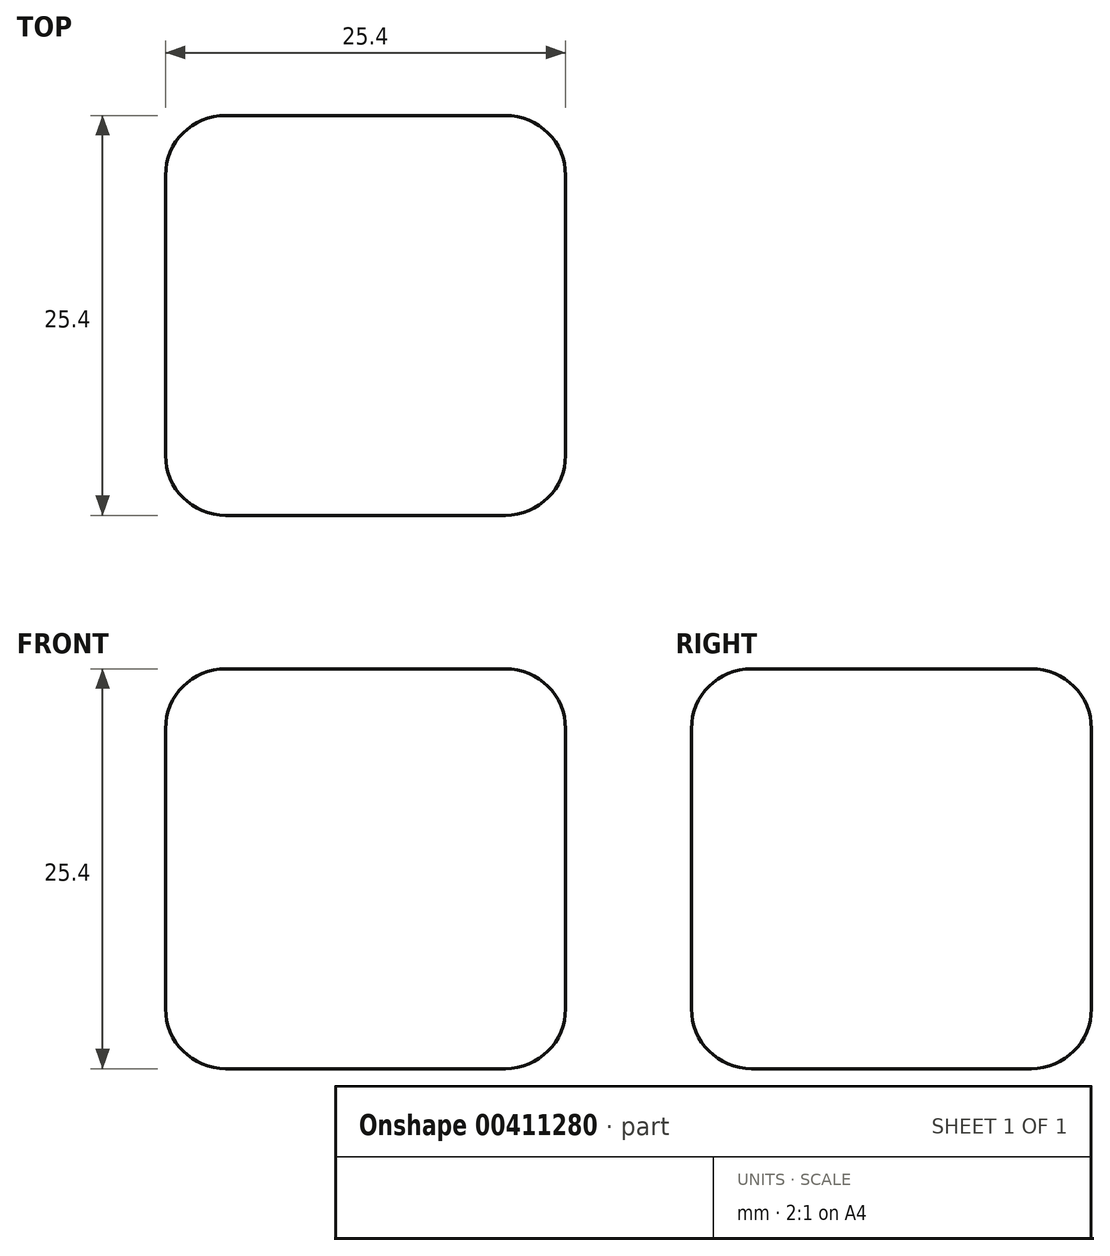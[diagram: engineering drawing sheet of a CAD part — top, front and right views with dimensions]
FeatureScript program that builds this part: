
annotation { "Feature Type Name" : "Feature", "Feature Type Description" : "" }
export const myFeature = defineFeature(function(context is Context, id is Id, definition is map)
    precondition{}
    {
        {
            var Q0;
            Q0=qCreatedBy(makeId("Top.planeOp"),FACE);
            var sketch = newSketch(context, id + "F0", { "sketchPlane" : qUnion([Q0])});
            skLineSegment(sketch, "E0.bottom", {"start": v(0, 0) * mm, "end": v(25.4, 0) * mm});
            skLineSegment(sketch, "E0.top", {"start": v(0, -25.4) * mm, "end": v(25.4, -25.4) * mm});
            skLineSegment(sketch, "E0.left", {"start": v(0, 0) * mm, "end": v(0, -25.4) * mm});
            skLineSegment(sketch, "E0.right", {"start": v(25.4, 0) * mm, "end": v(25.4, -25.4) * mm});
            skSolve(sketch);
        }
        {
            var Q0;
            Q0 = qSketchRegion(id + "F0", true);
            extrude(context, id + "F1", {"entities" : qUnion([Q0]), "depth" : 25.4 * mm});
        }
        {
            var Q0;
            Q0=makeQuery(id+"F1.opExtrude","SWEPT_EDGE",EDGE,{"disambiguationData":[OSD([sQuery(id+"F0.wireOp",EDGE,"E0.bottom"),sQuery(id+"F0.wireOp",EDGE,"E0.left")])]});
            var Q1;
            Q1=makeQuery(id+"F1.opExtrude","CAP_EDGE",EDGE,{"disambiguationData":[OSD([sQuery(id+"F0.wireOp",EDGE,"E0.bottom")])],"isStart":false});
            var Q2;
            Q2=makeQuery(id+"F1.opExtrude","CAP_EDGE",EDGE,{"disambiguationData":[OSD([sQuery(id+"F0.wireOp",EDGE,"E0.top")])],"isStart":false});
            var Q3;
            Q3=makeQuery(id+"F1.opExtrude","CAP_EDGE",EDGE,{"disambiguationData":[OSD([sQuery(id+"F0.wireOp",EDGE,"E0.bottom")])],"isStart":true});
            var Q4;
            Q4=makeQuery(id+"F1.opExtrude","SWEPT_EDGE",EDGE,{"disambiguationData":[OSD([sQuery(id+"F0.wireOp",EDGE,"E0.bottom"),sQuery(id+"F0.wireOp",EDGE,"E0.right")])]});
            var Q5;
            Q5=makeQuery(id+"F1.opExtrude","CAP_EDGE",EDGE,{"disambiguationData":[OSD([sQuery(id+"F0.wireOp",EDGE,"E0.left")])],"isStart":false});
            var Q6;
            Q6=makeQuery(id+"F1.opExtrude","CAP_EDGE",EDGE,{"disambiguationData":[OSD([sQuery(id+"F0.wireOp",EDGE,"E0.right")])],"isStart":false});
            var Q7;
            Q7=makeQuery(id+"F1.opExtrude","SWEPT_EDGE",EDGE,{"disambiguationData":[OSD([sQuery(id+"F0.wireOp",EDGE,"E0.top"),sQuery(id+"F0.wireOp",EDGE,"E0.right")])]});
            var Q8;
            Q8=makeQuery(id+"F1.opExtrude","CAP_EDGE",EDGE,{"disambiguationData":[OSD([sQuery(id+"F0.wireOp",EDGE,"E0.right")])],"isStart":true});
            var Q9;
            Q9=makeQuery(id+"F1.opExtrude","CAP_EDGE",EDGE,{"disambiguationData":[OSD([sQuery(id+"F0.wireOp",EDGE,"E0.top")])],"isStart":true});
            var Q10;
            Q10=makeQuery(id+"F1.opExtrude","SWEPT_FACE",FACE,{"disambiguationData":[OSD([sQuery(id+"F0.wireOp",EDGE,"E0.left")])]});
            fillet(context, id + "F2", {"entities" : qUnion([Q0, Q1, Q2, Q3, Q4, Q5, Q6, Q7, Q8, Q9, Q10]), "radius" : 3.8 * mm, "tangentPropagation" : true, "allowEdgeOverflow" : false});
        }
    });
